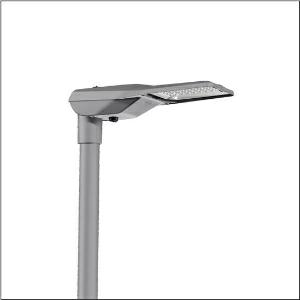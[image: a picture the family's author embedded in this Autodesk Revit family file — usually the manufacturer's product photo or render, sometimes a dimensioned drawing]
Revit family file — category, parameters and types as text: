
# Revit family: streetlight_sl_21_iq_mini___st1_0a_5xe2d51y08hb_d8f2
name_source: partatom
category: Lighting Fixtures
units: mm (PartAtom-declared; Revit-internal decimal feet)

## family parameters
Cut with Voids When Loaded = No
Host = Face
Light Source = No
Part Type = Normal
Room Calculation Point = No
Round Connector Dimension = Use Diameter
Shared = No

## types (1)
- --- (1 x LED, 8560 lm, 71 W, 3000K)
    Apparent Load = 71 VA
    CIE Flux Codes = 37 72 97 100 100
    Color Rendering = 80
    Color Temperature = 3000K
    Default Elevation = 1800 mm
    Description = Streetlight SL 21 iQ mini, mast luminaire, primary light control with lens, of PMMA, primary optical cover: cover, of toughened safety glass, transparent, light distribution: ST1.0a, light emission: direct distribution, primary light characteristic: asymmetric, installation type: post-top, side-entry, LED, High Power LED, rated luminous flux: 8.560lm, luminous efficacy: 121lm/W, light colour: 830, colour temperature: 3000K, control gear: iQ-Street Remote, D4i with power reduction, control: pre-setting: logarithmic dimming characteristic, Street-Remote, Auto-Match, Temp-Guard, Lumen-Switch, Night-Set, Smart-Wire, Light-Fading, Desk-Remote (wireless, voltage-free reading and setting of iQ features in the workshop via application-optimized NFC function/RFID function), optimised constant luminous flux control (CLO 2.0), mains connection: 220..240V, AC, 50/60Hz, start of lifetime: 71W, end of service life: 75W, reduction: 30W, luminaire housing, of diecast aluminium, powder-coated, SITECO metallic grey (DB 702S), corrosivity category C5 high according to DIN EN ISO 12944, please order mast flange separately, inclination adjustable: 0°, 5°, 10°, 15°, sealing non-destructively replaceable, multi-level sealing system, length: 628mm, width: 235mm, height: 110mm, mast flange for spigot size: 42mm (side-entry): 5XC10008XM4, 60/48mm (side-entry/post-top): 5XC10108XM2, 76/60mm (side-entry/post-top): 5XC10108XM1, mounting height: 4..8m, Smart Interface below and above, protection rating (complete): IP66, insulation class (complete): insulation class II (safety insulation), certification: CE, ENEC, ENEC+, VDE, impact resistance: IK10, permissible operating ambient temperature for outdoor applications: -40..+50°C, standard-compliant lighting for roads and squares, packaging unit: 1 piece

Light Distribution: ST1.0a
    Height = 110 mm
    Lamp = 1 x LED
    Lamp Light Flux = 8560 lm
    Lamp Power = 71 W
    Lamp count = 1
    Length = 625 mm
    Luminous efficacy = 121 lm/W
    Manufacturer = Siteco
    ModVariant = No
    Model = 5XE2D51Y08HB
    Mounting Place = Pole
    Mounting Type = Pole top
    Number of Poles = 1
    OnlyDefault = Yes
    Power Factor = 1
    Product Name = Streetlight SL 21 iQ mini | ST1.0a
    Product group = mast luminaire | pylon top
    ProductGroupID = 6100
    Protection Class = Protection class II
    Protection Degree = IP 66
    RLX_Detail_Level = 1
    RLX_Emergency_Light_Flux = 0 lm
    RLX_Emergency_Type = 0
    RLX_Emergency_Type_DB = No
    RlxData = <blob elided: 92573 chars, md5=34d26c8d>
    Socket = socket
    Standby Power = 0 W
    System Light Flux = 8560 lm
    System Power = 71 W
    Type Comments = factory setting: luminous flux: 100 % | dim-lin: 254 | 716 mA
    Type Image = l_1003514.jpg
    URL = http://relux.com
    VarID = @adj_116477
    Voltage = 0 V
    Weight = 0.00 kg
    Width = 234 mm

## geometry (parser evidence)
native form markers: Blend x4, Sweep x13
no freeform markers — native parametric forms only
